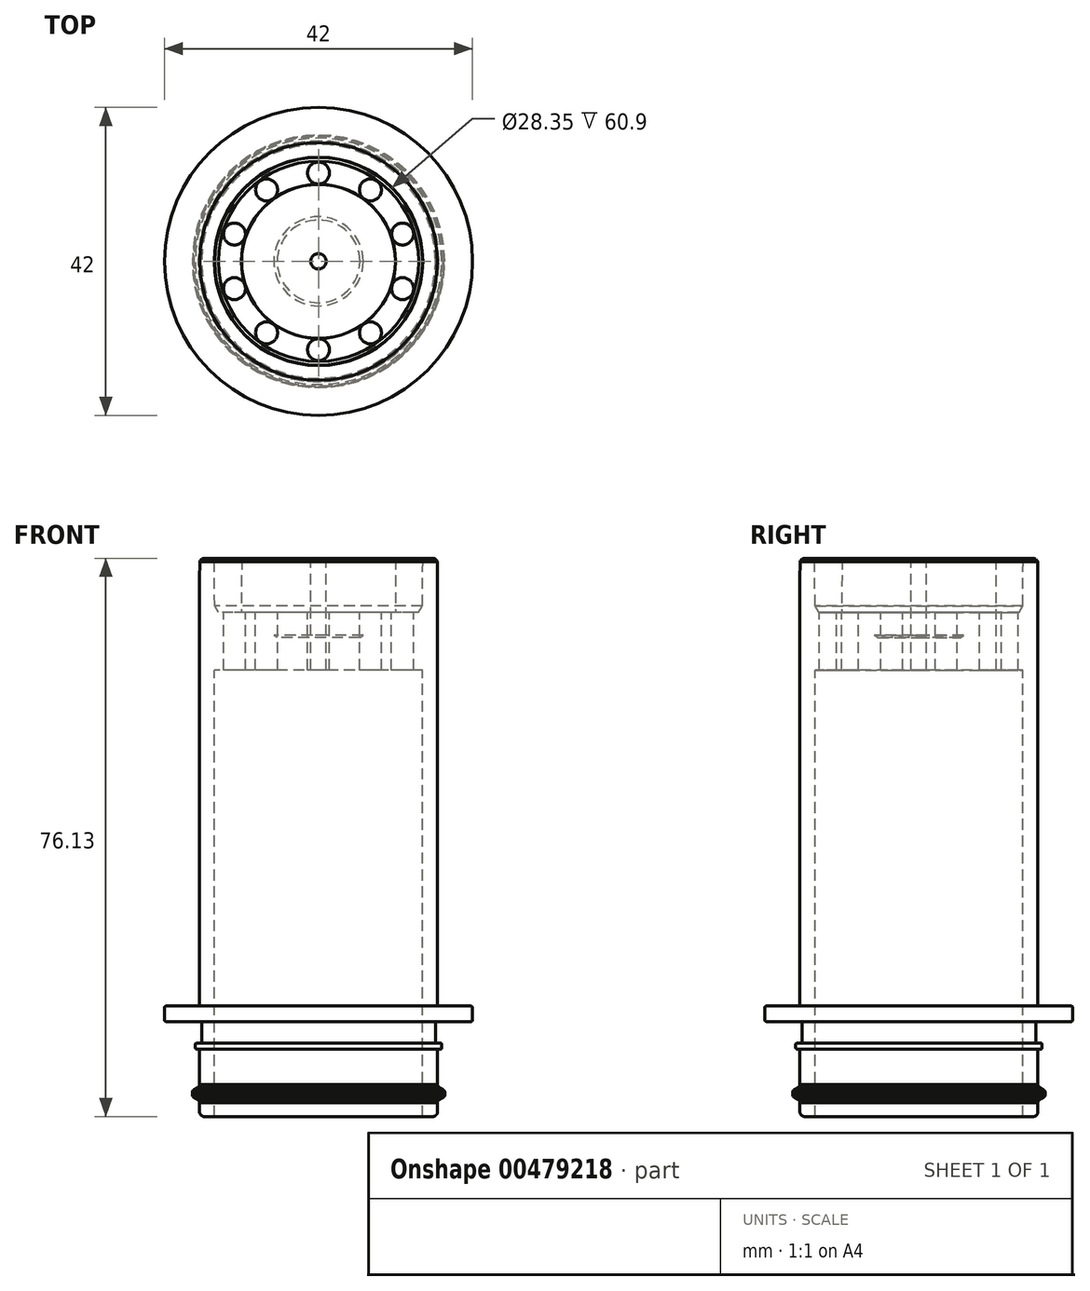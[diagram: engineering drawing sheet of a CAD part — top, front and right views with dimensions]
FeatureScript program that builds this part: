
annotation { "Feature Type Name" : "Feature", "Feature Type Description" : "" }
export const myFeature = defineFeature(function(context is Context, id is Id, definition is map)
    precondition{}
    {
        {
            var Q0;
            Q0=qCreatedBy(makeId("Front.planeOp"),FACE);
            var sketch = newSketch(context, id + "F0", { "sketchPlane" : qUnion([Q0])});
            skLineSegment(sketch, "E0", {"start": v(1.05, 34.13) * mm, "end": v(1.05, 26.78) * mm});
            skLineSegment(sketch, "E1", {"start": v(-1.05, 26.78) * mm, "end": v(-1.05, 34.13) * mm});
            skLineSegment(sketch, "E2", {"start": v(-1.05, 26.78) * mm, "end": v(-1.05, 16.7) * mm});
            skLineSegment(sketch, "E3", {"start": v(1.05, 16.7) * mm, "end": v(1.05, 26.78) * mm});
            skEllipticalArc(sketch, "E4", {});
            skLineSegment(sketch, "E5", {"start": v(1.05, 27.67) * mm, "end": v(-1.05, 27.67) * mm});
            skLineSegment(sketch, "E6", {"start": v(-16.24, 28.88) * mm, "end": v(-16.2, 34.13) * mm});
            skLineSegment(sketch, "E7", {"start": v(-13.65, 26.78) * mm, "end": v(-10.5, 26.78) * mm});
            skLineSegment(sketch, "E8", {"start": v(-14.16, 27.67) * mm, "end": v(-14.22, 34.13) * mm});
            skLineSegment(sketch, "E9", {"start": v(-10.48, 34.12) * mm, "end": v(-10.51, 26.78) * mm});
            skLineSegment(sketch, "E10", {"start": v(16.24, 28.88) * mm, "end": v(16.2, 34.13) * mm});
            skLineSegment(sketch, "E11", {"start": v(13.65, 26.78) * mm, "end": v(10.5, 26.78) * mm});
            skLineSegment(sketch, "E12", {"start": v(14.16, 27.67) * mm, "end": v(14.22, 34.13) * mm});
            skLineSegment(sketch, "E13", {"start": v(10.48, 34.1) * mm, "end": v(10.51, 26.78) * mm});
            skLineSegment(sketch, "E14", {"start": v(13.65, 26.78) * mm, "end": v(14.16, 27.67) * mm});
            skLineSegment(sketch, "E15", {"start": v(-13.65, 26.78) * mm, "end": v(-14.16, 27.67) * mm});
            skLineSegment(sketch, "E16", {"start": v(20.8, -26.94) * mm, "end": v(16.43, -26.94) * mm});
            skLineSegment(sketch, "E17", {"start": v(16.14, -29.04) * mm, "end": v(20.8, -29.04) * mm});
            skLineSegment(sketch, "E18", {"start": v(16.28, 28.88) * mm, "end": v(16.24, 28.88) * mm});
            skLineSegment(sketch, "E19", {"start": v(-16.24, 28.88) * mm, "end": v(-16.28, 28.88) * mm});
            skLineSegment(sketch, "E20", {"start": v(16.97, -38.3) * mm, "end": v(16.97, -38.3) * mm});
            skLineSegment(sketch, "E21", {"start": v(16.97, -38.3) * mm, "end": v(16.98, -38.3) * mm});
            skLineSegment(sketch, "E22", {"start": v(16.98, -38.3) * mm, "end": v(16.98, -38.3) * mm});
            skLineSegment(sketch, "E23", {"start": v(16.98, -38.3) * mm, "end": v(16.98, -38.31) * mm});
            skLineSegment(sketch, "E24", {"start": v(16.98, -38.31) * mm, "end": v(16.98, -38.31) * mm});
            skLineSegment(sketch, "E25", {"start": v(16.98, -38.31) * mm, "end": v(16.99, -38.31) * mm});
            skLineSegment(sketch, "E26", {"start": v(16.99, -38.31) * mm, "end": v(16.99, -38.31) * mm});
            skLineSegment(sketch, "E27", {"start": v(16.99, -38.31) * mm, "end": v(16.99, -38.32) * mm});
            skLineSegment(sketch, "E28", {"start": v(-16.4, -38.02) * mm, "end": v(-16.41, -38.01) * mm});
            skLineSegment(sketch, "E29", {"start": v(-16.41, -38.01) * mm, "end": v(-16.42, -38) * mm});
            skLineSegment(sketch, "E30", {"start": v(-16.42, -38) * mm, "end": v(-16.43, -38) * mm});
            skLineSegment(sketch, "E31", {"start": v(-16.43, -38) * mm, "end": v(-16.44, -38) * mm});
            skLineSegment(sketch, "E32", {"start": v(-16.44, -38) * mm, "end": v(-16.44, -38) * mm});
            skLineSegment(sketch, "E33", {"start": v(-16.44, -38) * mm, "end": v(-16.45, -37.99) * mm});
            skLineSegment(sketch, "E34", {"start": v(-16.45, -37.99) * mm, "end": v(-16.46, -37.98) * mm});
            skLineSegment(sketch, "E35", {"start": v(-16.46, -37.98) * mm, "end": v(-16.47, -37.98) * mm});
            skLineSegment(sketch, "E36", {"start": v(-16.47, -37.98) * mm, "end": v(-16.48, -37.97) * mm});
            skLineSegment(sketch, "E37", {"start": v(-16.48, -37.97) * mm, "end": v(-16.48, -37.97) * mm});
            skLineSegment(sketch, "E38", {"start": v(-16.48, -37.97) * mm, "end": v(-16.5, -37.97) * mm});
            skLineSegment(sketch, "E39", {"start": v(-16.5, -37.97) * mm, "end": v(-16.5, -37.96) * mm});
            skLineSegment(sketch, "E40", {"start": v(-16.5, -37.96) * mm, "end": v(-16.5, -37.96) * mm});
            skLineSegment(sketch, "E41", {"start": v(-16.5, -37.96) * mm, "end": v(-16.52, -37.95) * mm});
            skLineSegment(sketch, "E42", {"start": v(-16.52, -37.95) * mm, "end": v(-16.52, -37.95) * mm});
            skLineSegment(sketch, "E43", {"start": v(-16.52, -37.95) * mm, "end": v(-16.53, -37.94) * mm});
            skLineSegment(sketch, "E44", {"start": v(-16.53, -37.94) * mm, "end": v(-16.54, -37.94) * mm});
            skLineSegment(sketch, "E45", {"start": v(-16.54, -37.94) * mm, "end": v(-16.55, -37.93) * mm});
            skLineSegment(sketch, "E46", {"start": v(-16.55, -37.93) * mm, "end": v(-16.55, -37.93) * mm});
            skLineSegment(sketch, "E47", {"start": v(-16.55, -37.93) * mm, "end": v(-16.56, -37.92) * mm});
            skLineSegment(sketch, "E48", {"start": v(-16.56, -37.92) * mm, "end": v(-16.57, -37.92) * mm});
            skLineSegment(sketch, "E49", {"start": v(-16.57, -37.92) * mm, "end": v(-16.58, -37.91) * mm});
            skLineSegment(sketch, "E50", {"start": v(-16.58, -37.91) * mm, "end": v(-16.59, -37.91) * mm});
            skLineSegment(sketch, "E51", {"start": v(-16.59, -37.91) * mm, "end": v(-16.6, -37.9) * mm});
            skLineSegment(sketch, "E52", {"start": v(16.4, -37.98) * mm, "end": v(16.43, -38) * mm});
            skLineSegment(sketch, "E53", {"start": v(16.43, -38) * mm, "end": v(16.45, -38) * mm});
            skLineSegment(sketch, "E54", {"start": v(16.45, -38) * mm, "end": v(16.48, -38.02) * mm});
            skLineSegment(sketch, "E55", {"start": v(16.48, -38.02) * mm, "end": v(16.5, -38.03) * mm});
            skLineSegment(sketch, "E56", {"start": v(16.5, -38.03) * mm, "end": v(16.52, -38.05) * mm});
            skLineSegment(sketch, "E57", {"start": v(16.52, -38.05) * mm, "end": v(16.55, -38.06) * mm});
            skLineSegment(sketch, "E58", {"start": v(16.55, -38.06) * mm, "end": v(16.57, -38.07) * mm});
            skLineSegment(sketch, "E59", {"start": v(16.57, -38.07) * mm, "end": v(16.6, -38.09) * mm});
            skLineSegment(sketch, "E60", {"start": v(16.6, -38.09) * mm, "end": v(16.62, -38.1) * mm});
            skLineSegment(sketch, "E61", {"start": v(16.62, -38.1) * mm, "end": v(16.64, -38.11) * mm});
            skLineSegment(sketch, "E62", {"start": v(16.64, -38.11) * mm, "end": v(16.66, -38.13) * mm});
            skLineSegment(sketch, "E63", {"start": v(16.66, -38.13) * mm, "end": v(16.69, -38.14) * mm});
            skLineSegment(sketch, "E64", {"start": v(16.69, -38.14) * mm, "end": v(16.71, -38.16) * mm});
            skLineSegment(sketch, "E65", {"start": v(16.71, -38.16) * mm, "end": v(16.74, -38.17) * mm});
            skLineSegment(sketch, "E66", {"start": v(16.74, -38.17) * mm, "end": v(16.76, -38.18) * mm});
            skLineSegment(sketch, "E67", {"start": v(16.76, -38.18) * mm, "end": v(16.78, -38.2) * mm});
            skLineSegment(sketch, "E68", {"start": v(16.78, -38.2) * mm, "end": v(16.8, -38.21) * mm});
            skLineSegment(sketch, "E69", {"start": v(16.8, -38.21) * mm, "end": v(16.83, -38.22) * mm});
            skLineSegment(sketch, "E70", {"start": v(16.83, -38.22) * mm, "end": v(16.85, -38.24) * mm});
            skLineSegment(sketch, "E71", {"start": v(16.85, -38.24) * mm, "end": v(16.88, -38.25) * mm});
            skLineSegment(sketch, "E72", {"start": v(16.88, -38.25) * mm, "end": v(16.9, -38.27) * mm});
            skLineSegment(sketch, "E73", {"start": v(16.9, -38.27) * mm, "end": v(16.93, -38.28) * mm});
            skLineSegment(sketch, "E74", {"start": v(16.93, -38.28) * mm, "end": v(16.95, -38.3) * mm});
            skLineSegment(sketch, "E75", {"start": v(16.95, -38.3) * mm, "end": v(16.97, -38.3) * mm});
            skLineSegment(sketch, "E76", {"start": v(17, -38.34) * mm, "end": v(17, -38.34) * mm});
            skLineSegment(sketch, "E77", {"start": v(17, -38.34) * mm, "end": v(17, -38.33) * mm});
            skLineSegment(sketch, "E78", {"start": v(17, -38.33) * mm, "end": v(17, -38.33) * mm});
            skLineSegment(sketch, "E79", {"start": v(17, -38.33) * mm, "end": v(17, -38.32) * mm});
            skLineSegment(sketch, "E80", {"start": v(17, -38.32) * mm, "end": v(17, -38.32) * mm});
            skLineSegment(sketch, "E81", {"start": v(17, -38.32) * mm, "end": v(16.99, -38.32) * mm});
            skLineSegment(sketch, "E82", {"start": v(16.99, -38.32) * mm, "end": v(16.99, -38.32) * mm});
            skLineSegment(sketch, "E83", {"start": v(16.99, -38.32) * mm, "end": v(16.99, -38.31) * mm});
            skLineSegment(sketch, "E84", {"start": v(16.99, -38.31) * mm, "end": v(16.98, -38.31) * mm});
            skLineSegment(sketch, "E85", {"start": v(16.98, -38.31) * mm, "end": v(16.98, -38.3) * mm});
            skLineSegment(sketch, "E86", {"start": v(16.98, -38.3) * mm, "end": v(16.97, -38.3) * mm});
            skLineSegment(sketch, "E87", {"start": v(14.18, -42) * mm, "end": v(-14.18, -42) * mm});
            skLineSegment(sketch, "E88", {"start": v(0, 23.63) * mm, "end": v(-6.09, 23.63) * mm});
            skLineSegment(sketch, "E89", {"start": v(-5.64, 23.31) * mm, "end": v(0, 23.31) * mm});
            skLineSegment(sketch, "E90", {"start": v(0, 23.63) * mm, "end": v(0, 23.31) * mm});
            skLineSegment(sketch, "E91", {"start": v(6.09, 23.63) * mm, "end": v(0, 23.63) * mm});
            skLineSegment(sketch, "E92", {"start": v(0, 23.31) * mm, "end": v(5.64, 23.31) * mm});
            skLineSegment(sketch, "E93", {"start": v(1.05, 33.5) * mm, "end": v(10.48, 33.45) * mm});
            skLineSegment(sketch, "E94", {"start": v(-10.48, 33.48) * mm, "end": v(-1.05, 33.5) * mm});
            skLineSegment(sketch, "E95", {"start": v(-14.22, 34.13) * mm, "end": v(-16.2, 34.13) * mm});
            skLineSegment(sketch, "E96", {"start": v(-1.05, 34.13) * mm, "end": v(-10.48, 34.12) * mm});
            skLineSegment(sketch, "E97", {"start": v(10.48, 34.1) * mm, "end": v(1.05, 34.13) * mm});
            skLineSegment(sketch, "E98", {"start": v(16.2, 34.13) * mm, "end": v(14.22, 34.13) * mm});
            skLineSegment(sketch, "E99", {"start": v(0, 23.31) * mm, "end": v(0, 18.9) * mm});
            skLineSegment(sketch, "E100", {"start": v(0, 18.9) * mm, "end": v(-5.64, 18.9) * mm});
            skLineSegment(sketch, "E101", {"start": v(5.64, 18.9) * mm, "end": v(0, 18.9) * mm});
            skLineSegment(sketch, "E102", {"start": v(-16.22, -38.35) * mm, "end": v(-16.23, -38.32) * mm});
            skLineSegment(sketch, "E103", {"start": v(-16.23, -38.32) * mm, "end": v(-16.23, -38.3) * mm});
            skLineSegment(sketch, "E104", {"start": v(-16.23, -38.3) * mm, "end": v(-16.24, -38.28) * mm});
            skLineSegment(sketch, "E105", {"start": v(-16.24, -38.28) * mm, "end": v(-16.25, -38.26) * mm});
            skLineSegment(sketch, "E106", {"start": v(-16.25, -38.26) * mm, "end": v(-16.25, -38.23) * mm});
            skLineSegment(sketch, "E107", {"start": v(-16.25, -38.23) * mm, "end": v(-16.26, -38.2) * mm});
            skLineSegment(sketch, "E108", {"start": v(-16.26, -38.2) * mm, "end": v(-16.27, -38.19) * mm});
            skLineSegment(sketch, "E109", {"start": v(-16.27, -38.19) * mm, "end": v(-16.27, -38.16) * mm});
            skLineSegment(sketch, "E110", {"start": v(-16.27, -38.16) * mm, "end": v(-16.28, -38.14) * mm});
            skLineSegment(sketch, "E111", {"start": v(-16.28, -38.14) * mm, "end": v(-16.29, -38.13) * mm});
            skLineSegment(sketch, "E112", {"start": v(-16.29, -38.13) * mm, "end": v(-16.3, -38.12) * mm});
            skLineSegment(sketch, "E113", {"start": v(-16.3, -38.12) * mm, "end": v(-16.3, -38.1) * mm});
            skLineSegment(sketch, "E114", {"start": v(-16.3, -38.1) * mm, "end": v(-16.32, -38.1) * mm});
            skLineSegment(sketch, "E115", {"start": v(-16.32, -38.1) * mm, "end": v(-16.33, -38.08) * mm});
            skLineSegment(sketch, "E116", {"start": v(-16.33, -38.08) * mm, "end": v(-16.34, -38.07) * mm});
            skLineSegment(sketch, "E117", {"start": v(-16.34, -38.07) * mm, "end": v(-16.35, -38.06) * mm});
            skLineSegment(sketch, "E118", {"start": v(-16.35, -38.06) * mm, "end": v(-16.36, -38.05) * mm});
            skLineSegment(sketch, "E119", {"start": v(-16.36, -38.05) * mm, "end": v(-16.36, -38.05) * mm});
            skLineSegment(sketch, "E120", {"start": v(-16.36, -38.05) * mm, "end": v(-16.37, -38.04) * mm});
            skLineSegment(sketch, "E121", {"start": v(-16.37, -38.04) * mm, "end": v(-16.38, -38.04) * mm});
            skLineSegment(sketch, "E122", {"start": v(-16.38, -38.04) * mm, "end": v(-16.38, -38.03) * mm});
            skLineSegment(sketch, "E123", {"start": v(-16.38, -38.03) * mm, "end": v(-16.4, -38.03) * mm});
            skLineSegment(sketch, "E124", {"start": v(-16.4, -38.03) * mm, "end": v(-16.4, -38.02) * mm});
            skLineSegment(sketch, "E125", {"start": v(-16.4, -38.02) * mm, "end": v(-16.4, -38.02) * mm});
            skLineSegment(sketch, "E126", {"start": v(16.22, -37.65) * mm, "end": v(16.23, -37.67) * mm});
            skLineSegment(sketch, "E127", {"start": v(16.23, -37.67) * mm, "end": v(16.23, -37.7) * mm});
            skLineSegment(sketch, "E128", {"start": v(16.23, -37.7) * mm, "end": v(16.24, -37.71) * mm});
            skLineSegment(sketch, "E129", {"start": v(16.24, -37.71) * mm, "end": v(16.25, -37.74) * mm});
            skLineSegment(sketch, "E130", {"start": v(16.25, -37.74) * mm, "end": v(16.25, -37.76) * mm});
            skLineSegment(sketch, "E131", {"start": v(16.25, -37.76) * mm, "end": v(16.26, -37.78) * mm});
            skLineSegment(sketch, "E132", {"start": v(16.26, -37.78) * mm, "end": v(16.27, -37.8) * mm});
            skLineSegment(sketch, "E133", {"start": v(16.27, -37.8) * mm, "end": v(16.27, -37.83) * mm});
            skLineSegment(sketch, "E134", {"start": v(16.27, -37.83) * mm, "end": v(16.28, -37.85) * mm});
            skLineSegment(sketch, "E135", {"start": v(16.28, -37.85) * mm, "end": v(16.29, -37.86) * mm});
            skLineSegment(sketch, "E136", {"start": v(16.29, -37.86) * mm, "end": v(16.3, -37.87) * mm});
            skLineSegment(sketch, "E137", {"start": v(16.3, -37.87) * mm, "end": v(16.3, -37.89) * mm});
            skLineSegment(sketch, "E138", {"start": v(16.3, -37.89) * mm, "end": v(16.32, -37.9) * mm});
            skLineSegment(sketch, "E139", {"start": v(16.32, -37.9) * mm, "end": v(16.33, -37.91) * mm});
            skLineSegment(sketch, "E140", {"start": v(16.33, -37.91) * mm, "end": v(16.34, -37.92) * mm});
            skLineSegment(sketch, "E141", {"start": v(16.34, -37.92) * mm, "end": v(16.35, -37.94) * mm});
            skLineSegment(sketch, "E142", {"start": v(16.35, -37.94) * mm, "end": v(16.36, -37.94) * mm});
            skLineSegment(sketch, "E143", {"start": v(16.36, -37.94) * mm, "end": v(16.36, -37.95) * mm});
            skLineSegment(sketch, "E144", {"start": v(16.36, -37.95) * mm, "end": v(16.37, -37.95) * mm});
            skLineSegment(sketch, "E145", {"start": v(16.37, -37.95) * mm, "end": v(16.38, -37.96) * mm});
            skLineSegment(sketch, "E146", {"start": v(16.38, -37.96) * mm, "end": v(16.38, -37.96) * mm});
            skLineSegment(sketch, "E147", {"start": v(16.38, -37.96) * mm, "end": v(16.4, -37.97) * mm});
            skLineSegment(sketch, "E148", {"start": v(16.4, -37.97) * mm, "end": v(16.4, -37.97) * mm});
            skLineSegment(sketch, "E149", {"start": v(16.4, -37.97) * mm, "end": v(16.4, -37.98) * mm});
            skLineSegment(sketch, "E150", {"start": v(-16.43, -37.98) * mm, "end": v(-16.43, -37.98) * mm});
            skLineSegment(sketch, "E151", {"start": v(-16.43, -37.98) * mm, "end": v(-16.43, -37.99) * mm});
            skLineSegment(sketch, "E152", {"start": v(-16.43, -37.99) * mm, "end": v(-16.43, -37.99) * mm});
            skLineSegment(sketch, "E153", {"start": v(-16.43, -37.99) * mm, "end": v(-16.43, -38) * mm});
            skLineSegment(sketch, "E154", {"start": v(-16.43, -38) * mm, "end": v(-16.43, -38) * mm});
            skLineSegment(sketch, "E155", {"start": v(-16.43, -38) * mm, "end": v(-16.42, -38) * mm});
            skLineSegment(sketch, "E156", {"start": v(-16.42, -38) * mm, "end": v(-16.42, -38) * mm});
            skLineSegment(sketch, "E157", {"start": v(-16.42, -38) * mm, "end": v(-16.41, -38) * mm});
            skLineSegment(sketch, "E158", {"start": v(-16.41, -38) * mm, "end": v(-16.41, -38.01) * mm});
            skLineSegment(sketch, "E159", {"start": v(-16.41, -38.01) * mm, "end": v(-16.41, -38.01) * mm});
            skLineSegment(sketch, "E160", {"start": v(-16.41, -38.01) * mm, "end": v(-16.4, -38.01) * mm});
            skLineSegment(sketch, "E161", {"start": v(-16.4, -38.01) * mm, "end": v(-16.4, -38.01) * mm});
            skLineSegment(sketch, "E162", {"start": v(-16.4, -38.01) * mm, "end": v(-16.4, -38.02) * mm});
            skLineSegment(sketch, "E163", {"start": v(16.43, -38.01) * mm, "end": v(16.43, -38) * mm});
            skLineSegment(sketch, "E164", {"start": v(16.43, -38) * mm, "end": v(16.43, -38) * mm});
            skLineSegment(sketch, "E165", {"start": v(16.43, -38) * mm, "end": v(16.42, -38) * mm});
            skLineSegment(sketch, "E166", {"start": v(16.42, -38) * mm, "end": v(16.42, -38) * mm});
            skLineSegment(sketch, "E167", {"start": v(16.42, -38) * mm, "end": v(16.42, -37.99) * mm});
            skLineSegment(sketch, "E168", {"start": v(16.42, -37.99) * mm, "end": v(16.42, -37.99) * mm});
            skLineSegment(sketch, "E169", {"start": v(16.42, -37.99) * mm, "end": v(16.41, -37.98) * mm});
            skLineSegment(sketch, "E170", {"start": v(16.41, -37.98) * mm, "end": v(16.41, -37.98) * mm});
            skLineSegment(sketch, "E171", {"start": v(16.41, -37.98) * mm, "end": v(16.4, -37.98) * mm});
            skLineSegment(sketch, "E172", {"start": v(16.4, -37.98) * mm, "end": v(16.4, -37.98) * mm});
            skLineSegment(sketch, "E173", {"start": v(-14.18, 23.63) * mm, "end": v(-14.18, 33.5) * mm});
            skLineSegment(sketch, "E174", {"start": v(-6.09, 23.63) * mm, "end": v(-14.18, 23.63) * mm});
            skLineSegment(sketch, "E175", {"start": v(-6.09, 23.63) * mm, "end": v(-5.64, 23.31) * mm});
            skLineSegment(sketch, "E176", {"start": v(-5.64, 23.31) * mm, "end": v(-5.64, 18.9) * mm});
            skLineSegment(sketch, "E177", {"start": v(-14.18, 18.9) * mm, "end": v(-5.64, 18.9) * mm});
            skLineSegment(sketch, "E178", {"start": v(-14.18, -42) * mm, "end": v(-14.18, 18.9) * mm});
            skLineSegment(sketch, "E179", {"start": v(-15.6, -42) * mm, "end": v(-14.18, -42) * mm});
            skArc(sketch, "E180", {"start": v(-16.22, -41.37) * mm, "mid": v(-16.04, -41.82) * mm, "end": v(-15.6, -42) * mm});
            skLineSegment(sketch, "E181", {"start": v(-16.22, -38.35) * mm, "end": v(-16.22, -41.37) * mm});
            skLineSegment(sketch, "E182", {"start": v(-16.43, -37.98) * mm, "end": v(-16.42, -38) * mm});
            skLineSegment(sketch, "E183", {"start": v(-16.42, -38) * mm, "end": v(-16.4, -38) * mm});
            skLineSegment(sketch, "E184", {"start": v(-16.4, -38) * mm, "end": v(-16.39, -38.01) * mm});
            skLineSegment(sketch, "E185", {"start": v(-16.39, -38.01) * mm, "end": v(-16.37, -38.03) * mm});
            skLineSegment(sketch, "E186", {"start": v(-16.37, -38.03) * mm, "end": v(-16.36, -38.04) * mm});
            skLineSegment(sketch, "E187", {"start": v(-16.36, -38.04) * mm, "end": v(-16.35, -38.05) * mm});
            skLineSegment(sketch, "E188", {"start": v(-16.35, -38.05) * mm, "end": v(-16.33, -38.06) * mm});
            skLineSegment(sketch, "E189", {"start": v(-16.33, -38.06) * mm, "end": v(-16.32, -38.08) * mm});
            skLineSegment(sketch, "E190", {"start": v(-16.32, -38.08) * mm, "end": v(-16.3, -38.1) * mm});
            skLineSegment(sketch, "E191", {"start": v(-16.3, -38.1) * mm, "end": v(-16.3, -38.1) * mm});
            skLineSegment(sketch, "E192", {"start": v(-16.3, -38.1) * mm, "end": v(-16.29, -38.12) * mm});
            skLineSegment(sketch, "E193", {"start": v(-16.29, -38.12) * mm, "end": v(-16.28, -38.14) * mm});
            skLineSegment(sketch, "E194", {"start": v(-16.28, -38.14) * mm, "end": v(-16.27, -38.15) * mm});
            skLineSegment(sketch, "E195", {"start": v(-16.27, -38.15) * mm, "end": v(-16.26, -38.17) * mm});
            skLineSegment(sketch, "E196", {"start": v(-16.26, -38.17) * mm, "end": v(-16.25, -38.19) * mm});
            skLineSegment(sketch, "E197", {"start": v(-16.25, -38.19) * mm, "end": v(-16.25, -38.2) * mm});
            skLineSegment(sketch, "E198", {"start": v(-16.25, -38.2) * mm, "end": v(-16.24, -38.22) * mm});
            skLineSegment(sketch, "E199", {"start": v(-16.24, -38.22) * mm, "end": v(-16.24, -38.24) * mm});
            skLineSegment(sketch, "E200", {"start": v(-16.24, -38.24) * mm, "end": v(-16.23, -38.26) * mm});
            skLineSegment(sketch, "E201", {"start": v(-16.23, -38.26) * mm, "end": v(-16.23, -38.27) * mm});
            skLineSegment(sketch, "E202", {"start": v(-16.23, -38.27) * mm, "end": v(-16.23, -38.3) * mm});
            skLineSegment(sketch, "E203", {"start": v(-16.23, -38.3) * mm, "end": v(-16.22, -38.31) * mm});
            skLineSegment(sketch, "E204", {"start": v(-16.22, -38.31) * mm, "end": v(-16.22, -38.33) * mm});
            skLineSegment(sketch, "E205", {"start": v(-16.22, -38.33) * mm, "end": v(-16.22, -38.35) * mm});
            skLineSegment(sketch, "E206", {"start": v(-17, -37.66) * mm, "end": v(-16.98, -37.67) * mm});
            skLineSegment(sketch, "E207", {"start": v(-16.98, -37.67) * mm, "end": v(-16.95, -37.68) * mm});
            skLineSegment(sketch, "E208", {"start": v(-16.95, -37.68) * mm, "end": v(-16.93, -37.7) * mm});
            skLineSegment(sketch, "E209", {"start": v(-16.93, -37.7) * mm, "end": v(-16.9, -37.71) * mm});
            skLineSegment(sketch, "E210", {"start": v(-16.9, -37.71) * mm, "end": v(-16.88, -37.72) * mm});
            skLineSegment(sketch, "E211", {"start": v(-16.88, -37.72) * mm, "end": v(-16.86, -37.74) * mm});
            skLineSegment(sketch, "E212", {"start": v(-16.86, -37.74) * mm, "end": v(-16.83, -37.75) * mm});
            skLineSegment(sketch, "E213", {"start": v(-16.83, -37.75) * mm, "end": v(-16.81, -37.76) * mm});
            skLineSegment(sketch, "E214", {"start": v(-16.81, -37.76) * mm, "end": v(-16.79, -37.78) * mm});
            skLineSegment(sketch, "E215", {"start": v(-16.79, -37.78) * mm, "end": v(-16.76, -37.8) * mm});
            skLineSegment(sketch, "E216", {"start": v(-16.76, -37.8) * mm, "end": v(-16.74, -37.8) * mm});
            skLineSegment(sketch, "E217", {"start": v(-16.74, -37.8) * mm, "end": v(-16.72, -37.82) * mm});
            skLineSegment(sketch, "E218", {"start": v(-16.72, -37.82) * mm, "end": v(-16.7, -37.83) * mm});
            skLineSegment(sketch, "E219", {"start": v(-16.7, -37.83) * mm, "end": v(-16.67, -37.85) * mm});
            skLineSegment(sketch, "E220", {"start": v(-16.67, -37.85) * mm, "end": v(-16.65, -37.86) * mm});
            skLineSegment(sketch, "E221", {"start": v(-16.65, -37.86) * mm, "end": v(-16.62, -37.87) * mm});
            skLineSegment(sketch, "E222", {"start": v(-16.62, -37.87) * mm, "end": v(-16.6, -37.89) * mm});
            skLineSegment(sketch, "E223", {"start": v(-16.6, -37.89) * mm, "end": v(-16.57, -37.9) * mm});
            skLineSegment(sketch, "E224", {"start": v(-16.57, -37.9) * mm, "end": v(-16.55, -37.92) * mm});
            skLineSegment(sketch, "E225", {"start": v(-16.55, -37.92) * mm, "end": v(-16.53, -37.93) * mm});
            skLineSegment(sketch, "E226", {"start": v(-16.53, -37.93) * mm, "end": v(-16.5, -37.94) * mm});
            skLineSegment(sketch, "E227", {"start": v(-16.5, -37.94) * mm, "end": v(-16.48, -37.96) * mm});
            skLineSegment(sketch, "E228", {"start": v(-16.48, -37.96) * mm, "end": v(-16.46, -37.97) * mm});
            skLineSegment(sketch, "E229", {"start": v(-16.46, -37.97) * mm, "end": v(-16.43, -37.98) * mm});
            skLineSegment(sketch, "E230", {"start": v(-17.2, -37.3) * mm, "end": v(-17.2, -37.31) * mm});
            skLineSegment(sketch, "E231", {"start": v(-17.2, -37.31) * mm, "end": v(-17.2, -37.33) * mm});
            skLineSegment(sketch, "E232", {"start": v(-17.2, -37.33) * mm, "end": v(-17.2, -37.35) * mm});
            skLineSegment(sketch, "E233", {"start": v(-17.2, -37.35) * mm, "end": v(-17.2, -37.37) * mm});
            skLineSegment(sketch, "E234", {"start": v(-17.2, -37.37) * mm, "end": v(-17.2, -37.38) * mm});
            skLineSegment(sketch, "E235", {"start": v(-17.2, -37.38) * mm, "end": v(-17.2, -37.4) * mm});
            skLineSegment(sketch, "E236", {"start": v(-17.2, -37.4) * mm, "end": v(-17.2, -37.42) * mm});
            skLineSegment(sketch, "E237", {"start": v(-17.2, -37.42) * mm, "end": v(-17.18, -37.44) * mm});
            skLineSegment(sketch, "E238", {"start": v(-17.18, -37.44) * mm, "end": v(-17.18, -37.45) * mm});
            skLineSegment(sketch, "E239", {"start": v(-17.18, -37.45) * mm, "end": v(-17.17, -37.47) * mm});
            skLineSegment(sketch, "E240", {"start": v(-17.17, -37.47) * mm, "end": v(-17.16, -37.49) * mm});
            skLineSegment(sketch, "E241", {"start": v(-17.16, -37.49) * mm, "end": v(-17.15, -37.5) * mm});
            skLineSegment(sketch, "E242", {"start": v(-17.15, -37.5) * mm, "end": v(-17.14, -37.52) * mm});
            skLineSegment(sketch, "E243", {"start": v(-17.14, -37.52) * mm, "end": v(-17.13, -37.53) * mm});
            skLineSegment(sketch, "E244", {"start": v(-17.13, -37.53) * mm, "end": v(-17.12, -37.55) * mm});
            skLineSegment(sketch, "E245", {"start": v(-17.12, -37.55) * mm, "end": v(-17.11, -37.56) * mm});
            skLineSegment(sketch, "E246", {"start": v(-17.11, -37.56) * mm, "end": v(-17.1, -37.58) * mm});
            skLineSegment(sketch, "E247", {"start": v(-17.1, -37.58) * mm, "end": v(-17.09, -37.59) * mm});
            skLineSegment(sketch, "E248", {"start": v(-17.09, -37.59) * mm, "end": v(-17.07, -37.6) * mm});
            skLineSegment(sketch, "E249", {"start": v(-17.07, -37.6) * mm, "end": v(-17.06, -37.61) * mm});
            skLineSegment(sketch, "E250", {"start": v(-17.06, -37.61) * mm, "end": v(-17.05, -37.63) * mm});
            skLineSegment(sketch, "E251", {"start": v(-17.05, -37.63) * mm, "end": v(-17.03, -37.64) * mm});
            skLineSegment(sketch, "E252", {"start": v(-17.03, -37.64) * mm, "end": v(-17.02, -37.65) * mm});
            skLineSegment(sketch, "E253", {"start": v(-17.02, -37.65) * mm, "end": v(-17, -37.66) * mm});
            skLineSegment(sketch, "E254", {"start": v(-17.2, -36.96) * mm, "end": v(-17.2, -37.3) * mm});
            skLineSegment(sketch, "E255", {"start": v(-17, -36.6) * mm, "end": v(-17.02, -36.6) * mm});
            skLineSegment(sketch, "E256", {"start": v(-17.02, -36.6) * mm, "end": v(-17.03, -36.61) * mm});
            skLineSegment(sketch, "E257", {"start": v(-17.03, -36.61) * mm, "end": v(-17.05, -36.62) * mm});
            skLineSegment(sketch, "E258", {"start": v(-17.05, -36.62) * mm, "end": v(-17.06, -36.64) * mm});
            skLineSegment(sketch, "E259", {"start": v(-17.06, -36.64) * mm, "end": v(-17.07, -36.65) * mm});
            skLineSegment(sketch, "E260", {"start": v(-17.07, -36.65) * mm, "end": v(-17.09, -36.66) * mm});
            skLineSegment(sketch, "E261", {"start": v(-17.09, -36.66) * mm, "end": v(-17.1, -36.67) * mm});
            skLineSegment(sketch, "E262", {"start": v(-17.1, -36.67) * mm, "end": v(-17.11, -36.69) * mm});
            skLineSegment(sketch, "E263", {"start": v(-17.11, -36.69) * mm, "end": v(-17.12, -36.7) * mm});
            skLineSegment(sketch, "E264", {"start": v(-17.12, -36.7) * mm, "end": v(-17.13, -36.72) * mm});
            skLineSegment(sketch, "E265", {"start": v(-17.13, -36.72) * mm, "end": v(-17.14, -36.73) * mm});
            skLineSegment(sketch, "E266", {"start": v(-17.14, -36.73) * mm, "end": v(-17.15, -36.75) * mm});
            skLineSegment(sketch, "E267", {"start": v(-17.15, -36.75) * mm, "end": v(-17.16, -36.76) * mm});
            skLineSegment(sketch, "E268", {"start": v(-17.16, -36.76) * mm, "end": v(-17.17, -36.78) * mm});
            skLineSegment(sketch, "E269", {"start": v(-17.17, -36.78) * mm, "end": v(-17.18, -36.8) * mm});
            skLineSegment(sketch, "E270", {"start": v(-17.18, -36.8) * mm, "end": v(-17.18, -36.81) * mm});
            skLineSegment(sketch, "E271", {"start": v(-17.18, -36.81) * mm, "end": v(-17.2, -36.83) * mm});
            skLineSegment(sketch, "E272", {"start": v(-17.2, -36.83) * mm, "end": v(-17.2, -36.85) * mm});
            skLineSegment(sketch, "E273", {"start": v(-17.2, -36.85) * mm, "end": v(-17.2, -36.87) * mm});
            skLineSegment(sketch, "E274", {"start": v(-17.2, -36.87) * mm, "end": v(-17.2, -36.89) * mm});
            skLineSegment(sketch, "E275", {"start": v(-17.2, -36.89) * mm, "end": v(-17.2, -36.9) * mm});
            skLineSegment(sketch, "E276", {"start": v(-17.2, -36.9) * mm, "end": v(-17.2, -36.92) * mm});
            skLineSegment(sketch, "E277", {"start": v(-17.2, -36.92) * mm, "end": v(-17.2, -36.94) * mm});
            skLineSegment(sketch, "E278", {"start": v(-17.2, -36.94) * mm, "end": v(-17.2, -36.96) * mm});
            skLineSegment(sketch, "E279", {"start": v(-16.43, -36.27) * mm, "end": v(-16.46, -36.28) * mm});
            skLineSegment(sketch, "E280", {"start": v(-16.46, -36.28) * mm, "end": v(-16.48, -36.3) * mm});
            skLineSegment(sketch, "E281", {"start": v(-16.48, -36.3) * mm, "end": v(-16.5, -36.3) * mm});
            skLineSegment(sketch, "E282", {"start": v(-16.5, -36.3) * mm, "end": v(-16.53, -36.32) * mm});
            skLineSegment(sketch, "E283", {"start": v(-16.53, -36.32) * mm, "end": v(-16.55, -36.34) * mm});
            skLineSegment(sketch, "E284", {"start": v(-16.55, -36.34) * mm, "end": v(-16.57, -36.35) * mm});
            skLineSegment(sketch, "E285", {"start": v(-16.57, -36.35) * mm, "end": v(-16.6, -36.36) * mm});
            skLineSegment(sketch, "E286", {"start": v(-16.6, -36.36) * mm, "end": v(-16.62, -36.38) * mm});
            skLineSegment(sketch, "E287", {"start": v(-16.62, -36.38) * mm, "end": v(-16.65, -36.39) * mm});
            skLineSegment(sketch, "E288", {"start": v(-16.65, -36.39) * mm, "end": v(-16.67, -36.4) * mm});
            skLineSegment(sketch, "E289", {"start": v(-16.67, -36.4) * mm, "end": v(-16.7, -36.42) * mm});
            skLineSegment(sketch, "E290", {"start": v(-16.7, -36.42) * mm, "end": v(-16.72, -36.43) * mm});
            skLineSegment(sketch, "E291", {"start": v(-16.72, -36.43) * mm, "end": v(-16.74, -36.44) * mm});
            skLineSegment(sketch, "E292", {"start": v(-16.74, -36.44) * mm, "end": v(-16.76, -36.46) * mm});
            skLineSegment(sketch, "E293", {"start": v(-16.76, -36.46) * mm, "end": v(-16.79, -36.47) * mm});
            skLineSegment(sketch, "E294", {"start": v(-16.79, -36.47) * mm, "end": v(-16.81, -36.49) * mm});
            skLineSegment(sketch, "E295", {"start": v(-16.81, -36.49) * mm, "end": v(-16.83, -36.5) * mm});
            skLineSegment(sketch, "E296", {"start": v(-16.83, -36.5) * mm, "end": v(-16.86, -36.51) * mm});
            skLineSegment(sketch, "E297", {"start": v(-16.86, -36.51) * mm, "end": v(-16.88, -36.53) * mm});
            skLineSegment(sketch, "E298", {"start": v(-16.88, -36.53) * mm, "end": v(-16.9, -36.54) * mm});
            skLineSegment(sketch, "E299", {"start": v(-16.9, -36.54) * mm, "end": v(-16.93, -36.55) * mm});
            skLineSegment(sketch, "E300", {"start": v(-16.93, -36.55) * mm, "end": v(-16.95, -36.57) * mm});
            skLineSegment(sketch, "E301", {"start": v(-16.95, -36.57) * mm, "end": v(-16.98, -36.58) * mm});
            skLineSegment(sketch, "E302", {"start": v(-16.98, -36.58) * mm, "end": v(-17, -36.6) * mm});
            skLineSegment(sketch, "E303", {"start": v(-16.22, -35.9) * mm, "end": v(-16.22, -35.92) * mm});
            skLineSegment(sketch, "E304", {"start": v(-16.22, -35.92) * mm, "end": v(-16.22, -35.94) * mm});
            skLineSegment(sketch, "E305", {"start": v(-16.22, -35.94) * mm, "end": v(-16.23, -35.96) * mm});
            skLineSegment(sketch, "E306", {"start": v(-16.23, -35.96) * mm, "end": v(-16.23, -35.98) * mm});
            skLineSegment(sketch, "E307", {"start": v(-16.23, -35.98) * mm, "end": v(-16.23, -36) * mm});
            skLineSegment(sketch, "E308", {"start": v(-16.23, -36) * mm, "end": v(-16.24, -36.01) * mm});
            skLineSegment(sketch, "E309", {"start": v(-16.24, -36.01) * mm, "end": v(-16.24, -36.03) * mm});
            skLineSegment(sketch, "E310", {"start": v(-16.24, -36.03) * mm, "end": v(-16.25, -36.05) * mm});
            skLineSegment(sketch, "E311", {"start": v(-16.25, -36.05) * mm, "end": v(-16.25, -36.06) * mm});
            skLineSegment(sketch, "E312", {"start": v(-16.25, -36.06) * mm, "end": v(-16.26, -36.08) * mm});
            skLineSegment(sketch, "E313", {"start": v(-16.26, -36.08) * mm, "end": v(-16.27, -36.1) * mm});
            skLineSegment(sketch, "E314", {"start": v(-16.27, -36.1) * mm, "end": v(-16.28, -36.11) * mm});
            skLineSegment(sketch, "E315", {"start": v(-16.28, -36.11) * mm, "end": v(-16.29, -36.13) * mm});
            skLineSegment(sketch, "E316", {"start": v(-16.29, -36.13) * mm, "end": v(-16.3, -36.14) * mm});
            skLineSegment(sketch, "E317", {"start": v(-16.3, -36.14) * mm, "end": v(-16.3, -36.16) * mm});
            skLineSegment(sketch, "E318", {"start": v(-16.3, -36.16) * mm, "end": v(-16.32, -36.17) * mm});
            skLineSegment(sketch, "E319", {"start": v(-16.32, -36.17) * mm, "end": v(-16.33, -36.19) * mm});
            skLineSegment(sketch, "E320", {"start": v(-16.33, -36.19) * mm, "end": v(-16.35, -36.2) * mm});
            skLineSegment(sketch, "E321", {"start": v(-16.35, -36.2) * mm, "end": v(-16.36, -36.21) * mm});
            skLineSegment(sketch, "E322", {"start": v(-16.36, -36.21) * mm, "end": v(-16.37, -36.23) * mm});
            skLineSegment(sketch, "E323", {"start": v(-16.37, -36.23) * mm, "end": v(-16.39, -36.24) * mm});
            skLineSegment(sketch, "E324", {"start": v(-16.39, -36.24) * mm, "end": v(-16.4, -36.25) * mm});
            skLineSegment(sketch, "E325", {"start": v(-16.4, -36.25) * mm, "end": v(-16.42, -36.26) * mm});
            skLineSegment(sketch, "E326", {"start": v(-16.42, -36.26) * mm, "end": v(-16.43, -36.27) * mm});
            skLineSegment(sketch, "E327", {"start": v(-16.22, -33.03) * mm, "end": v(-16.22, -35.9) * mm});
            skArc(sketch, "E328", {"start": v(-16.22, -33.03) * mm, "mid": v(-16.28, -32.88) * mm, "end": v(-16.43, -32.82) * mm});
            skLineSegment(sketch, "E329", {"start": v(-16.6, -32.82) * mm, "end": v(-16.43, -32.82) * mm});
            skArc(sketch, "E330", {"start": v(-16.8, -32.61) * mm, "mid": v(-16.74, -32.76) * mm, "end": v(-16.6, -32.82) * mm});
            skLineSegment(sketch, "E331", {"start": v(-16.8, -32.2) * mm, "end": v(-16.8, -32.61) * mm});
            skArc(sketch, "E332", {"start": v(-16.6, -31.98) * mm, "mid": v(-16.74, -32.04) * mm, "end": v(-16.8, -32.2) * mm});
            skLineSegment(sketch, "E333", {"start": v(-16.14, -31.98) * mm, "end": v(-16.6, -31.98) * mm});
            skArc(sketch, "E334", {"start": v(-16.14, -31.98) * mm, "mid": v(-16, -31.92) * mm, "end": v(-15.93, -31.77) * mm});
            skLineSegment(sketch, "E335", {"start": v(-15.93, -29.25) * mm, "end": v(-15.93, -31.77) * mm});
            skArc(sketch, "E336", {"start": v(-15.93, -29.25) * mm, "mid": v(-16, -29.1) * mm, "end": v(-16.14, -29.04) * mm});
            skLineSegment(sketch, "E337", {"start": v(-20.8, -29.04) * mm, "end": v(-16.14, -29.04) * mm});
            skArc(sketch, "E338", {"start": v(-21, -28.83) * mm, "mid": v(-20.94, -28.98) * mm, "end": v(-20.8, -29.04) * mm});
            skLineSegment(sketch, "E339", {"start": v(-21, -27.15) * mm, "end": v(-21, -28.83) * mm});
            skArc(sketch, "E340", {"start": v(-20.8, -26.94) * mm, "mid": v(-20.94, -27) * mm, "end": v(-21, -27.15) * mm});
            skLineSegment(sketch, "E341", {"start": v(-16.43, -26.94) * mm, "end": v(-20.8, -26.94) * mm});
            skArc(sketch, "E342", {"start": v(-16.43, -26.94) * mm, "mid": v(-16.28, -26.88) * mm, "end": v(-16.22, -26.73) * mm});
            skLineSegment(sketch, "E343", {"start": v(-16.22, 33.5) * mm, "end": v(-16.22, -26.73) * mm});
            skArc(sketch, "E344", {"start": v(-15.6, 34.13) * mm, "mid": v(-16.04, 33.94) * mm, "end": v(-16.22, 33.5) * mm});
            skLineSegment(sketch, "E345", {"start": v(-14.8, 34.13) * mm, "end": v(-15.6, 34.13) * mm});
            skArc(sketch, "E346", {"start": v(-14.18, 33.5) * mm, "mid": v(-14.36, 33.94) * mm, "end": v(-14.8, 34.13) * mm});
            skLineSegment(sketch, "E347", {"start": v(15.6, 34.13) * mm, "end": v(14.8, 34.13) * mm});
            skArc(sketch, "E348", {"start": v(16.22, 33.5) * mm, "mid": v(16.04, 33.94) * mm, "end": v(15.6, 34.13) * mm});
            skLineSegment(sketch, "E349", {"start": v(16.22, -26.73) * mm, "end": v(16.22, 33.5) * mm});
            skArc(sketch, "E350", {"start": v(16.22, -26.73) * mm, "mid": v(16.28, -26.88) * mm, "end": v(16.43, -26.94) * mm});
            skArc(sketch, "E351", {"start": v(16.14, -29.04) * mm, "mid": v(16, -29.1) * mm, "end": v(15.93, -29.25) * mm});
            skLineSegment(sketch, "E352", {"start": v(15.93, -31.77) * mm, "end": v(15.93, -29.25) * mm});
            skArc(sketch, "E353", {"start": v(15.93, -31.77) * mm, "mid": v(16, -31.92) * mm, "end": v(16.14, -31.98) * mm});
            skLineSegment(sketch, "E354", {"start": v(16.6, -31.98) * mm, "end": v(16.14, -31.98) * mm});
            skArc(sketch, "E355", {"start": v(16.8, -32.2) * mm, "mid": v(16.74, -32.04) * mm, "end": v(16.6, -31.98) * mm});
            skLineSegment(sketch, "E356", {"start": v(16.8, -32.61) * mm, "end": v(16.8, -32.2) * mm});
            skArc(sketch, "E357", {"start": v(16.6, -32.82) * mm, "mid": v(16.74, -32.76) * mm, "end": v(16.8, -32.61) * mm});
            skLineSegment(sketch, "E358", {"start": v(16.43, -32.82) * mm, "end": v(16.6, -32.82) * mm});
            skArc(sketch, "E359", {"start": v(16.43, -32.82) * mm, "mid": v(16.28, -32.88) * mm, "end": v(16.22, -33.03) * mm});
            skLineSegment(sketch, "E360", {"start": v(16.22, -37.65) * mm, "end": v(16.22, -33.03) * mm});
            skLineSegment(sketch, "E361", {"start": v(16.43, -38.01) * mm, "end": v(16.42, -38) * mm});
            skLineSegment(sketch, "E362", {"start": v(16.42, -38) * mm, "end": v(16.4, -38) * mm});
            skLineSegment(sketch, "E363", {"start": v(16.4, -38) * mm, "end": v(16.39, -37.98) * mm});
            skLineSegment(sketch, "E364", {"start": v(16.39, -37.98) * mm, "end": v(16.37, -37.97) * mm});
            skLineSegment(sketch, "E365", {"start": v(16.37, -37.97) * mm, "end": v(16.36, -37.96) * mm});
            skLineSegment(sketch, "E366", {"start": v(16.36, -37.96) * mm, "end": v(16.35, -37.94) * mm});
            skLineSegment(sketch, "E367", {"start": v(16.35, -37.94) * mm, "end": v(16.33, -37.93) * mm});
            skLineSegment(sketch, "E368", {"start": v(16.33, -37.93) * mm, "end": v(16.32, -37.92) * mm});
            skLineSegment(sketch, "E369", {"start": v(16.32, -37.92) * mm, "end": v(16.3, -37.9) * mm});
            skLineSegment(sketch, "E370", {"start": v(16.3, -37.9) * mm, "end": v(16.3, -37.89) * mm});
            skLineSegment(sketch, "E371", {"start": v(16.3, -37.89) * mm, "end": v(16.29, -37.87) * mm});
            skLineSegment(sketch, "E372", {"start": v(16.29, -37.87) * mm, "end": v(16.28, -37.86) * mm});
            skLineSegment(sketch, "E373", {"start": v(16.28, -37.86) * mm, "end": v(16.27, -37.84) * mm});
            skLineSegment(sketch, "E374", {"start": v(16.27, -37.84) * mm, "end": v(16.26, -37.82) * mm});
            skLineSegment(sketch, "E375", {"start": v(16.26, -37.82) * mm, "end": v(16.25, -37.8) * mm});
            skLineSegment(sketch, "E376", {"start": v(16.25, -37.8) * mm, "end": v(16.25, -37.79) * mm});
            skLineSegment(sketch, "E377", {"start": v(16.25, -37.79) * mm, "end": v(16.24, -37.77) * mm});
            skLineSegment(sketch, "E378", {"start": v(16.24, -37.77) * mm, "end": v(16.24, -37.75) * mm});
            skLineSegment(sketch, "E379", {"start": v(16.24, -37.75) * mm, "end": v(16.23, -37.74) * mm});
            skLineSegment(sketch, "E380", {"start": v(16.23, -37.74) * mm, "end": v(16.23, -37.72) * mm});
            skLineSegment(sketch, "E381", {"start": v(16.23, -37.72) * mm, "end": v(16.23, -37.7) * mm});
            skLineSegment(sketch, "E382", {"start": v(16.23, -37.7) * mm, "end": v(16.22, -37.68) * mm});
            skLineSegment(sketch, "E383", {"start": v(16.22, -37.68) * mm, "end": v(16.22, -37.66) * mm});
            skLineSegment(sketch, "E384", {"start": v(16.22, -37.66) * mm, "end": v(16.22, -37.65) * mm});
            skLineSegment(sketch, "E385", {"start": v(17, -38.34) * mm, "end": v(16.98, -38.32) * mm});
            skLineSegment(sketch, "E386", {"start": v(16.98, -38.32) * mm, "end": v(16.95, -38.31) * mm});
            skLineSegment(sketch, "E387", {"start": v(16.95, -38.31) * mm, "end": v(16.93, -38.3) * mm});
            skLineSegment(sketch, "E388", {"start": v(16.93, -38.3) * mm, "end": v(16.9, -38.28) * mm});
            skLineSegment(sketch, "E389", {"start": v(16.9, -38.28) * mm, "end": v(16.88, -38.27) * mm});
            skLineSegment(sketch, "E390", {"start": v(16.88, -38.27) * mm, "end": v(16.86, -38.26) * mm});
            skLineSegment(sketch, "E391", {"start": v(16.86, -38.26) * mm, "end": v(16.83, -38.24) * mm});
            skLineSegment(sketch, "E392", {"start": v(16.83, -38.24) * mm, "end": v(16.81, -38.23) * mm});
            skLineSegment(sketch, "E393", {"start": v(16.81, -38.23) * mm, "end": v(16.79, -38.21) * mm});
            skLineSegment(sketch, "E394", {"start": v(16.79, -38.21) * mm, "end": v(16.76, -38.2) * mm});
            skLineSegment(sketch, "E395", {"start": v(16.76, -38.2) * mm, "end": v(16.74, -38.19) * mm});
            skLineSegment(sketch, "E396", {"start": v(16.74, -38.19) * mm, "end": v(16.72, -38.17) * mm});
            skLineSegment(sketch, "E397", {"start": v(16.72, -38.17) * mm, "end": v(16.7, -38.16) * mm});
            skLineSegment(sketch, "E398", {"start": v(16.7, -38.16) * mm, "end": v(16.67, -38.15) * mm});
            skLineSegment(sketch, "E399", {"start": v(16.67, -38.15) * mm, "end": v(16.65, -38.13) * mm});
            skLineSegment(sketch, "E400", {"start": v(16.65, -38.13) * mm, "end": v(16.62, -38.12) * mm});
            skLineSegment(sketch, "E401", {"start": v(16.62, -38.12) * mm, "end": v(16.6, -38.1) * mm});
            skLineSegment(sketch, "E402", {"start": v(16.6, -38.1) * mm, "end": v(16.57, -38.1) * mm});
            skLineSegment(sketch, "E403", {"start": v(16.57, -38.1) * mm, "end": v(16.55, -38.08) * mm});
            skLineSegment(sketch, "E404", {"start": v(16.55, -38.08) * mm, "end": v(16.53, -38.06) * mm});
            skLineSegment(sketch, "E405", {"start": v(16.53, -38.06) * mm, "end": v(16.5, -38.05) * mm});
            skLineSegment(sketch, "E406", {"start": v(16.5, -38.05) * mm, "end": v(16.48, -38.04) * mm});
            skLineSegment(sketch, "E407", {"start": v(16.48, -38.04) * mm, "end": v(16.46, -38.02) * mm});
            skLineSegment(sketch, "E408", {"start": v(16.46, -38.02) * mm, "end": v(16.43, -38.01) * mm});
            skLineSegment(sketch, "E409", {"start": v(17.2, -38.7) * mm, "end": v(17.2, -38.68) * mm});
            skLineSegment(sketch, "E410", {"start": v(17.2, -38.68) * mm, "end": v(17.2, -38.66) * mm});
            skLineSegment(sketch, "E411", {"start": v(17.2, -38.66) * mm, "end": v(17.2, -38.65) * mm});
            skLineSegment(sketch, "E412", {"start": v(17.2, -38.65) * mm, "end": v(17.2, -38.63) * mm});
            skLineSegment(sketch, "E413", {"start": v(17.2, -38.63) * mm, "end": v(17.2, -38.61) * mm});
            skLineSegment(sketch, "E414", {"start": v(17.2, -38.61) * mm, "end": v(17.2, -38.6) * mm});
            skLineSegment(sketch, "E415", {"start": v(17.2, -38.6) * mm, "end": v(17.2, -38.57) * mm});
            skLineSegment(sketch, "E416", {"start": v(17.2, -38.57) * mm, "end": v(17.18, -38.56) * mm});
            skLineSegment(sketch, "E417", {"start": v(17.18, -38.56) * mm, "end": v(17.18, -38.54) * mm});
            skLineSegment(sketch, "E418", {"start": v(17.18, -38.54) * mm, "end": v(17.17, -38.52) * mm});
            skLineSegment(sketch, "E419", {"start": v(17.17, -38.52) * mm, "end": v(17.16, -38.5) * mm});
            skLineSegment(sketch, "E420", {"start": v(17.16, -38.5) * mm, "end": v(17.15, -38.5) * mm});
            skLineSegment(sketch, "E421", {"start": v(17.15, -38.5) * mm, "end": v(17.14, -38.48) * mm});
            skLineSegment(sketch, "E422", {"start": v(17.14, -38.48) * mm, "end": v(17.13, -38.46) * mm});
            skLineSegment(sketch, "E423", {"start": v(17.13, -38.46) * mm, "end": v(17.12, -38.45) * mm});
            skLineSegment(sketch, "E424", {"start": v(17.12, -38.45) * mm, "end": v(17.11, -38.43) * mm});
            skLineSegment(sketch, "E425", {"start": v(17.11, -38.43) * mm, "end": v(17.1, -38.42) * mm});
            skLineSegment(sketch, "E426", {"start": v(17.1, -38.42) * mm, "end": v(17.09, -38.4) * mm});
            skLineSegment(sketch, "E427", {"start": v(17.09, -38.4) * mm, "end": v(17.07, -38.4) * mm});
            skLineSegment(sketch, "E428", {"start": v(17.07, -38.4) * mm, "end": v(17.06, -38.38) * mm});
            skLineSegment(sketch, "E429", {"start": v(17.06, -38.38) * mm, "end": v(17.05, -38.37) * mm});
            skLineSegment(sketch, "E430", {"start": v(17.05, -38.37) * mm, "end": v(17.03, -38.36) * mm});
            skLineSegment(sketch, "E431", {"start": v(17.03, -38.36) * mm, "end": v(17.02, -38.35) * mm});
            skLineSegment(sketch, "E432", {"start": v(17.02, -38.35) * mm, "end": v(17, -38.34) * mm});
            skLineSegment(sketch, "E433", {"start": v(17.2, -39.04) * mm, "end": v(17.2, -38.7) * mm});
            skLineSegment(sketch, "E434", {"start": v(17, -39.4) * mm, "end": v(17.02, -39.39) * mm});
            skLineSegment(sketch, "E435", {"start": v(17.02, -39.39) * mm, "end": v(17.03, -39.38) * mm});
            skLineSegment(sketch, "E436", {"start": v(17.03, -39.38) * mm, "end": v(17.05, -39.37) * mm});
            skLineSegment(sketch, "E437", {"start": v(17.05, -39.37) * mm, "end": v(17.06, -39.36) * mm});
            skLineSegment(sketch, "E438", {"start": v(17.06, -39.36) * mm, "end": v(17.07, -39.34) * mm});
            skLineSegment(sketch, "E439", {"start": v(17.07, -39.34) * mm, "end": v(17.09, -39.33) * mm});
            skLineSegment(sketch, "E440", {"start": v(17.09, -39.33) * mm, "end": v(17.1, -39.32) * mm});
            skLineSegment(sketch, "E441", {"start": v(17.1, -39.32) * mm, "end": v(17.11, -39.3) * mm});
            skLineSegment(sketch, "E442", {"start": v(17.11, -39.3) * mm, "end": v(17.12, -39.3) * mm});
            skLineSegment(sketch, "E443", {"start": v(17.12, -39.3) * mm, "end": v(17.13, -39.28) * mm});
            skLineSegment(sketch, "E444", {"start": v(17.13, -39.28) * mm, "end": v(17.14, -39.26) * mm});
            skLineSegment(sketch, "E445", {"start": v(17.14, -39.26) * mm, "end": v(17.15, -39.25) * mm});
            skLineSegment(sketch, "E446", {"start": v(17.15, -39.25) * mm, "end": v(17.16, -39.23) * mm});
            skLineSegment(sketch, "E447", {"start": v(17.16, -39.23) * mm, "end": v(17.17, -39.21) * mm});
            skLineSegment(sketch, "E448", {"start": v(17.17, -39.21) * mm, "end": v(17.18, -39.2) * mm});
            skLineSegment(sketch, "E449", {"start": v(17.18, -39.2) * mm, "end": v(17.18, -39.18) * mm});
            skLineSegment(sketch, "E450", {"start": v(17.18, -39.18) * mm, "end": v(17.2, -39.16) * mm});
            skLineSegment(sketch, "E451", {"start": v(17.2, -39.16) * mm, "end": v(17.2, -39.14) * mm});
            skLineSegment(sketch, "E452", {"start": v(17.2, -39.14) * mm, "end": v(17.2, -39.13) * mm});
            skLineSegment(sketch, "E453", {"start": v(17.2, -39.13) * mm, "end": v(17.2, -39.1) * mm});
            skLineSegment(sketch, "E454", {"start": v(17.2, -39.1) * mm, "end": v(17.2, -39.09) * mm});
            skLineSegment(sketch, "E455", {"start": v(17.2, -39.09) * mm, "end": v(17.2, -39.07) * mm});
            skLineSegment(sketch, "E456", {"start": v(17.2, -39.07) * mm, "end": v(17.2, -39.05) * mm});
            skLineSegment(sketch, "E457", {"start": v(17.2, -39.05) * mm, "end": v(17.2, -39.04) * mm});
            skLineSegment(sketch, "E458", {"start": v(16.43, -39.73) * mm, "end": v(16.46, -39.71) * mm});
            skLineSegment(sketch, "E459", {"start": v(16.46, -39.71) * mm, "end": v(16.48, -39.7) * mm});
            skLineSegment(sketch, "E460", {"start": v(16.48, -39.7) * mm, "end": v(16.5, -39.69) * mm});
            skLineSegment(sketch, "E461", {"start": v(16.5, -39.69) * mm, "end": v(16.53, -39.67) * mm});
            skLineSegment(sketch, "E462", {"start": v(16.53, -39.67) * mm, "end": v(16.55, -39.66) * mm});
            skLineSegment(sketch, "E463", {"start": v(16.55, -39.66) * mm, "end": v(16.57, -39.64) * mm});
            skLineSegment(sketch, "E464", {"start": v(16.57, -39.64) * mm, "end": v(16.6, -39.63) * mm});
            skLineSegment(sketch, "E465", {"start": v(16.6, -39.63) * mm, "end": v(16.62, -39.62) * mm});
            skLineSegment(sketch, "E466", {"start": v(16.62, -39.62) * mm, "end": v(16.65, -39.6) * mm});
            skLineSegment(sketch, "E467", {"start": v(16.65, -39.6) * mm, "end": v(16.67, -39.59) * mm});
            skLineSegment(sketch, "E468", {"start": v(16.67, -39.59) * mm, "end": v(16.7, -39.58) * mm});
            skLineSegment(sketch, "E469", {"start": v(16.7, -39.58) * mm, "end": v(16.72, -39.56) * mm});
            skLineSegment(sketch, "E470", {"start": v(16.72, -39.56) * mm, "end": v(16.74, -39.55) * mm});
            skLineSegment(sketch, "E471", {"start": v(16.74, -39.55) * mm, "end": v(16.76, -39.54) * mm});
            skLineSegment(sketch, "E472", {"start": v(16.76, -39.54) * mm, "end": v(16.79, -39.52) * mm});
            skLineSegment(sketch, "E473", {"start": v(16.79, -39.52) * mm, "end": v(16.81, -39.5) * mm});
            skLineSegment(sketch, "E474", {"start": v(16.81, -39.5) * mm, "end": v(16.83, -39.5) * mm});
            skLineSegment(sketch, "E475", {"start": v(16.83, -39.5) * mm, "end": v(16.86, -39.48) * mm});
            skLineSegment(sketch, "E476", {"start": v(16.86, -39.48) * mm, "end": v(16.88, -39.47) * mm});
            skLineSegment(sketch, "E477", {"start": v(16.88, -39.47) * mm, "end": v(16.9, -39.45) * mm});
            skLineSegment(sketch, "E478", {"start": v(16.9, -39.45) * mm, "end": v(16.93, -39.44) * mm});
            skLineSegment(sketch, "E479", {"start": v(16.93, -39.44) * mm, "end": v(16.95, -39.43) * mm});
            skLineSegment(sketch, "E480", {"start": v(16.95, -39.43) * mm, "end": v(16.98, -39.41) * mm});
            skLineSegment(sketch, "E481", {"start": v(16.98, -39.41) * mm, "end": v(17, -39.4) * mm});
            skLineSegment(sketch, "E482", {"start": v(16.22, -40.1) * mm, "end": v(16.22, -40.07) * mm});
            skLineSegment(sketch, "E483", {"start": v(16.22, -40.07) * mm, "end": v(16.22, -40.05) * mm});
            skLineSegment(sketch, "E484", {"start": v(16.22, -40.05) * mm, "end": v(16.23, -40.04) * mm});
            skLineSegment(sketch, "E485", {"start": v(16.23, -40.04) * mm, "end": v(16.23, -40.02) * mm});
            skLineSegment(sketch, "E486", {"start": v(16.23, -40.02) * mm, "end": v(16.23, -40) * mm});
            skLineSegment(sketch, "E487", {"start": v(16.23, -40) * mm, "end": v(16.24, -39.98) * mm});
            skLineSegment(sketch, "E488", {"start": v(16.24, -39.98) * mm, "end": v(16.24, -39.96) * mm});
            skLineSegment(sketch, "E489", {"start": v(16.24, -39.96) * mm, "end": v(16.25, -39.95) * mm});
            skLineSegment(sketch, "E490", {"start": v(16.25, -39.95) * mm, "end": v(16.25, -39.93) * mm});
            skLineSegment(sketch, "E491", {"start": v(16.25, -39.93) * mm, "end": v(16.26, -39.91) * mm});
            skLineSegment(sketch, "E492", {"start": v(16.26, -39.91) * mm, "end": v(16.27, -39.9) * mm});
            skLineSegment(sketch, "E493", {"start": v(16.27, -39.9) * mm, "end": v(16.28, -39.88) * mm});
            skLineSegment(sketch, "E494", {"start": v(16.28, -39.88) * mm, "end": v(16.29, -39.86) * mm});
            skLineSegment(sketch, "E495", {"start": v(16.29, -39.86) * mm, "end": v(16.3, -39.85) * mm});
            skLineSegment(sketch, "E496", {"start": v(16.3, -39.85) * mm, "end": v(16.3, -39.83) * mm});
            skLineSegment(sketch, "E497", {"start": v(16.3, -39.83) * mm, "end": v(16.32, -39.82) * mm});
            skLineSegment(sketch, "E498", {"start": v(16.32, -39.82) * mm, "end": v(16.33, -39.8) * mm});
            skLineSegment(sketch, "E499", {"start": v(16.33, -39.8) * mm, "end": v(16.35, -39.8) * mm});
            skLineSegment(sketch, "E500", {"start": v(16.35, -39.8) * mm, "end": v(16.36, -39.78) * mm});
            skLineSegment(sketch, "E501", {"start": v(16.36, -39.78) * mm, "end": v(16.37, -39.77) * mm});
            skLineSegment(sketch, "E502", {"start": v(16.37, -39.77) * mm, "end": v(16.39, -39.76) * mm});
            skLineSegment(sketch, "E503", {"start": v(16.39, -39.76) * mm, "end": v(16.4, -39.75) * mm});
            skLineSegment(sketch, "E504", {"start": v(16.4, -39.75) * mm, "end": v(16.42, -39.74) * mm});
            skLineSegment(sketch, "E505", {"start": v(16.42, -39.74) * mm, "end": v(16.43, -39.73) * mm});
            skLineSegment(sketch, "E506", {"start": v(16.22, -41.37) * mm, "end": v(16.22, -40.1) * mm});
            skArc(sketch, "E507", {"start": v(15.6, -42) * mm, "mid": v(16.04, -41.82) * mm, "end": v(16.22, -41.37) * mm});
            skLineSegment(sketch, "E508", {"start": v(14.18, -42) * mm, "end": v(15.6, -42) * mm});
            skLineSegment(sketch, "E509", {"start": v(14.18, 18.9) * mm, "end": v(14.18, -42) * mm});
            skLineSegment(sketch, "E510", {"start": v(5.64, 18.9) * mm, "end": v(14.18, 18.9) * mm});
            skLineSegment(sketch, "E511", {"start": v(5.64, 23.31) * mm, "end": v(5.64, 18.9) * mm});
            skLineSegment(sketch, "E512", {"start": v(5.64, 23.31) * mm, "end": v(6.09, 23.63) * mm});
            skLineSegment(sketch, "E513", {"start": v(14.18, 23.63) * mm, "end": v(6.09, 23.63) * mm});
            skLineSegment(sketch, "E514", {"start": v(14.18, 33.5) * mm, "end": v(14.18, 23.63) * mm});
            skArc(sketch, "E515", {"start": v(14.8, 34.13) * mm, "mid": v(14.36, 33.94) * mm, "end": v(14.18, 33.5) * mm});
            skLineSegment(sketch, "E516", {"start": v(-16.64, -37.89) * mm, "end": v(-16.64, -37.89) * mm});
            skLineSegment(sketch, "E517", {"start": v(-16.64, -37.89) * mm, "end": v(-16.64, -37.9) * mm});
            skLineSegment(sketch, "E518", {"start": v(-16.64, -37.9) * mm, "end": v(-16.64, -37.9) * mm});
            skLineSegment(sketch, "E519", {"start": v(-16.64, -37.9) * mm, "end": v(-16.63, -37.9) * mm});
            skLineSegment(sketch, "E520", {"start": v(-16.63, -37.9) * mm, "end": v(-16.63, -37.9) * mm});
            skLineSegment(sketch, "E521", {"start": v(-16.63, -37.9) * mm, "end": v(-16.63, -37.91) * mm});
            skLineSegment(sketch, "E522", {"start": v(-16.63, -37.91) * mm, "end": v(-16.62, -37.91) * mm});
            skLineSegment(sketch, "E523", {"start": v(-16.62, -37.91) * mm, "end": v(-16.62, -37.92) * mm});
            skLineSegment(sketch, "E524", {"start": v(-16.62, -37.92) * mm, "end": v(-16.61, -37.92) * mm});
            skLineSegment(sketch, "E525", {"start": v(-16.61, -37.92) * mm, "end": v(-16.6, -37.92) * mm});
            skLineSegment(sketch, "E526", {"start": v(-16.6, -37.92) * mm, "end": v(-16.6, -37.92) * mm});
            skLineSegment(sketch, "E527", {"start": v(-16.6, -37.92) * mm, "end": v(-16.6, -37.93) * mm});
            skLineSegment(sketch, "E528", {"start": v(-16.6, -37.93) * mm, "end": v(-16.6, -37.93) * mm});
            skLineSegment(sketch, "E529", {"start": v(-16.6, -37.93) * mm, "end": v(-16.58, -37.93) * mm});
            skLineSegment(sketch, "E530", {"start": v(-16.58, -37.93) * mm, "end": v(-16.58, -37.93) * mm});
            skLineSegment(sketch, "E531", {"start": v(-16.58, -37.93) * mm, "end": v(-16.57, -37.94) * mm});
            skLineSegment(sketch, "E532", {"start": v(-16.57, -37.94) * mm, "end": v(-16.57, -37.94) * mm});
            skLineSegment(sketch, "E533", {"start": v(-16.57, -37.94) * mm, "end": v(-16.56, -37.94) * mm});
            skLineSegment(sketch, "E534", {"start": v(-16.56, -37.94) * mm, "end": v(-16.55, -37.94) * mm});
            skLineSegment(sketch, "E535", {"start": v(-16.55, -37.94) * mm, "end": v(-16.54, -37.95) * mm});
            skLineSegment(sketch, "E536", {"start": v(-16.54, -37.95) * mm, "end": v(-16.54, -37.95) * mm});
            skLineSegment(sketch, "E537", {"start": v(-16.54, -37.95) * mm, "end": v(-16.53, -37.95) * mm});
            skLineSegment(sketch, "E538", {"start": v(-16.53, -37.95) * mm, "end": v(-16.52, -37.95) * mm});
            skLineSegment(sketch, "E539", {"start": v(-16.52, -37.95) * mm, "end": v(-16.51, -37.96) * mm});
            skLineSegment(sketch, "E540", {"start": v(-16.51, -37.96) * mm, "end": v(-16.5, -37.96) * mm});
            skLineSegment(sketch, "E541", {"start": v(-17.6, -34.3) * mm, "end": v(-17.71, -34.3) * mm});
            skArc(sketch, "E542", {"start": v(21, -27.15) * mm, "mid": v(20.94, -27) * mm, "end": v(20.8, -26.94) * mm});
            skLineSegment(sketch, "E543", {"start": v(21, -28.83) * mm, "end": v(21, -27.15) * mm});
            skArc(sketch, "E544", {"start": v(20.8, -29.04) * mm, "mid": v(20.94, -28.98) * mm, "end": v(21, -28.83) * mm});
            skLineSegment(sketch, "E545", {"start": v(0, 46.98) * mm, "end": v(0, -116.7) * mm});
            const initialGuessF0  = {"E4": [0, 0.06370415100000001, 0, 1, 0.04706121000000001, 0.021945, 3.093727, 3.189458]};
            skSetInitialGuess(sketch, initialGuessF0);
            skSolve(sketch);
        }
        {
            var Q0;
            Q0=makeQuery(id+"F0.imprint","IMPRINT",FACE,{"disambiguationData":[TD([[makeQuery(id+"F0.imprint","IMPRINT",EDGE,{"derivedFrom":sQuery(id+"F0.wireOp",EDGE,"E16")}),1.0]])]});
            var Q1;
            {var subQ5=sQuery(id+"F0.wireOp",EDGE,"E511");Q1=makeQuery(id+"F0.imprint","IMPRINT",FACE,{"disambiguationData":[TD([[makeQuery(id+"F0.imprint","IMPRINT",EDGE,{"derivedFrom":subQ5}),-1.0]])]});}
            var Q2;
            {var subQ5=sQuery(id+"F0.wireOp",EDGE,"E13");Q2=makeQuery(id+"F0.imprint","IMPRINT",FACE,{"disambiguationData":[TD([[makeQuery(id+"F0.imprint","IMPRINT",EDGE,{"derivedFrom":subQ5}),-1.0]])]});}
            var Q3;
            {var subQ8=sQuery(id+"F0.wireOp",EDGE,"E14");Q3=makeQuery(id+"F0.imprint","IMPRINT",FACE,{"disambiguationData":[TD([[makeQuery(id+"F0.imprint","IMPRINT",EDGE,{"derivedFrom":subQ8}),-1.0]])]});}
            var Q4;
            Q4=sQuery(id+"F0.wireOp",EDGE,"E545");
            revolve(context, id + "F1", {"entities" : qUnion([Q0, Q1, Q2, Q3]), "axis" : qUnion([Q4]), "revolveType" : RevolveType.FULL});
        }
        {
            var Q0;
            Q0=makeQuery(id+"F1.opRevolve","SWEPT_FACE",FACE,{"disambiguationData":[OSD([sQuery(id+"F0.wireOp",EDGE,"E11")])]});
            var sketch = newSketch(context, id + "F2", { "sketchPlane" : qUnion([Q0])});
            skCircle(sketch, "E546", {"center": v(0, 12.05) * mm, "radius": 1.5 * mm});
            skPoint(sketch, "E547.center.orphan", {"position": v(0, 0) * mm});
            skCircle(sketch, "E548.1.0", {"center": v(-7.08, 9.75) * mm, "radius": 1.5 * mm});
            skCircle(sketch, "E548.2.0", {"center": v(-11.46, 3.72) * mm, "radius": 1.5 * mm});
            skCircle(sketch, "E548.3.0", {"center": v(-11.46, -3.72) * mm, "radius": 1.5 * mm});
            skCircle(sketch, "E548.4.0", {"center": v(-7.08, -9.75) * mm, "radius": 1.5 * mm});
            skCircle(sketch, "E548.5.0", {"center": v(0, -12.05) * mm, "radius": 1.5 * mm});
            skCircle(sketch, "E548.6.0", {"center": v(7.08, -9.75) * mm, "radius": 1.5 * mm});
            skCircle(sketch, "E548.7.0", {"center": v(11.46, -3.72) * mm, "radius": 1.5 * mm});
            skCircle(sketch, "E548.8.0", {"center": v(11.46, 3.72) * mm, "radius": 1.5 * mm});
            skCircle(sketch, "E548.9.0", {"center": v(7.08, 9.75) * mm, "radius": 1.5 * mm});
            skSolve(sketch);
        }
        {
            var Q0;
            Q0=makeQuery(id+"F2.imprint","IMPRINT",FACE,{"disambiguationData":[TD([[makeQuery(id+"F2.imprint","IMPRINT",EDGE,{"derivedFrom":sQuery(id+"F2.wireOp",EDGE,"E548.1.0")}),1.0]])]});
            var Q1;
            Q1=makeQuery(id+"F2.imprint","IMPRINT",FACE,{"disambiguationData":[TD([[makeQuery(id+"F2.imprint","IMPRINT",EDGE,{"derivedFrom":sQuery(id+"F2.wireOp",EDGE,"E546")}),1.0]])]});
            var Q2;
            Q2=makeQuery(id+"F2.imprint","IMPRINT",FACE,{"disambiguationData":[TD([[makeQuery(id+"F2.imprint","IMPRINT",EDGE,{"derivedFrom":sQuery(id+"F2.wireOp",EDGE,"E548.9.0")}),1.0]])]});
            var Q3;
            Q3=makeQuery(id+"F2.imprint","IMPRINT",FACE,{"disambiguationData":[TD([[makeQuery(id+"F2.imprint","IMPRINT",EDGE,{"derivedFrom":sQuery(id+"F2.wireOp",EDGE,"E548.8.0")}),1.0]])]});
            var Q4;
            Q4=makeQuery(id+"F2.imprint","IMPRINT",FACE,{"disambiguationData":[TD([[makeQuery(id+"F2.imprint","IMPRINT",EDGE,{"derivedFrom":sQuery(id+"F2.wireOp",EDGE,"E548.7.0")}),1.0]])]});
            var Q5;
            Q5=makeQuery(id+"F2.imprint","IMPRINT",FACE,{"disambiguationData":[TD([[makeQuery(id+"F2.imprint","IMPRINT",EDGE,{"derivedFrom":sQuery(id+"F2.wireOp",EDGE,"E548.6.0")}),1.0]])]});
            var Q6;
            Q6=makeQuery(id+"F2.imprint","IMPRINT",FACE,{"disambiguationData":[TD([[makeQuery(id+"F2.imprint","IMPRINT",EDGE,{"derivedFrom":sQuery(id+"F2.wireOp",EDGE,"E548.5.0")}),1.0]])]});
            var Q7;
            Q7=makeQuery(id+"F2.imprint","IMPRINT",FACE,{"disambiguationData":[TD([[makeQuery(id+"F2.imprint","IMPRINT",EDGE,{"derivedFrom":sQuery(id+"F2.wireOp",EDGE,"E548.4.0")}),1.0]])]});
            var Q8;
            Q8=makeQuery(id+"F2.imprint","IMPRINT",FACE,{"disambiguationData":[TD([[makeQuery(id+"F2.imprint","IMPRINT",EDGE,{"derivedFrom":sQuery(id+"F2.wireOp",EDGE,"E548.3.0")}),1.0]])]});
            var Q9;
            Q9=makeQuery(id+"F2.imprint","IMPRINT",FACE,{"disambiguationData":[TD([[makeQuery(id+"F2.imprint","IMPRINT",EDGE,{"derivedFrom":sQuery(id+"F2.wireOp",EDGE,"E548.2.0")}),1.0]])]});
            extrude(context, id + "F3", {"entities" : qUnion([Q0, Q1, Q2, Q3, Q4, Q5, Q6, Q7, Q8, Q9]), "operationType" : NewBodyOperationType.REMOVE, "oppositeDirection" : true, "depth" : 25 * mm, "offsetDistance" : 25 * mm});
        }
    });
